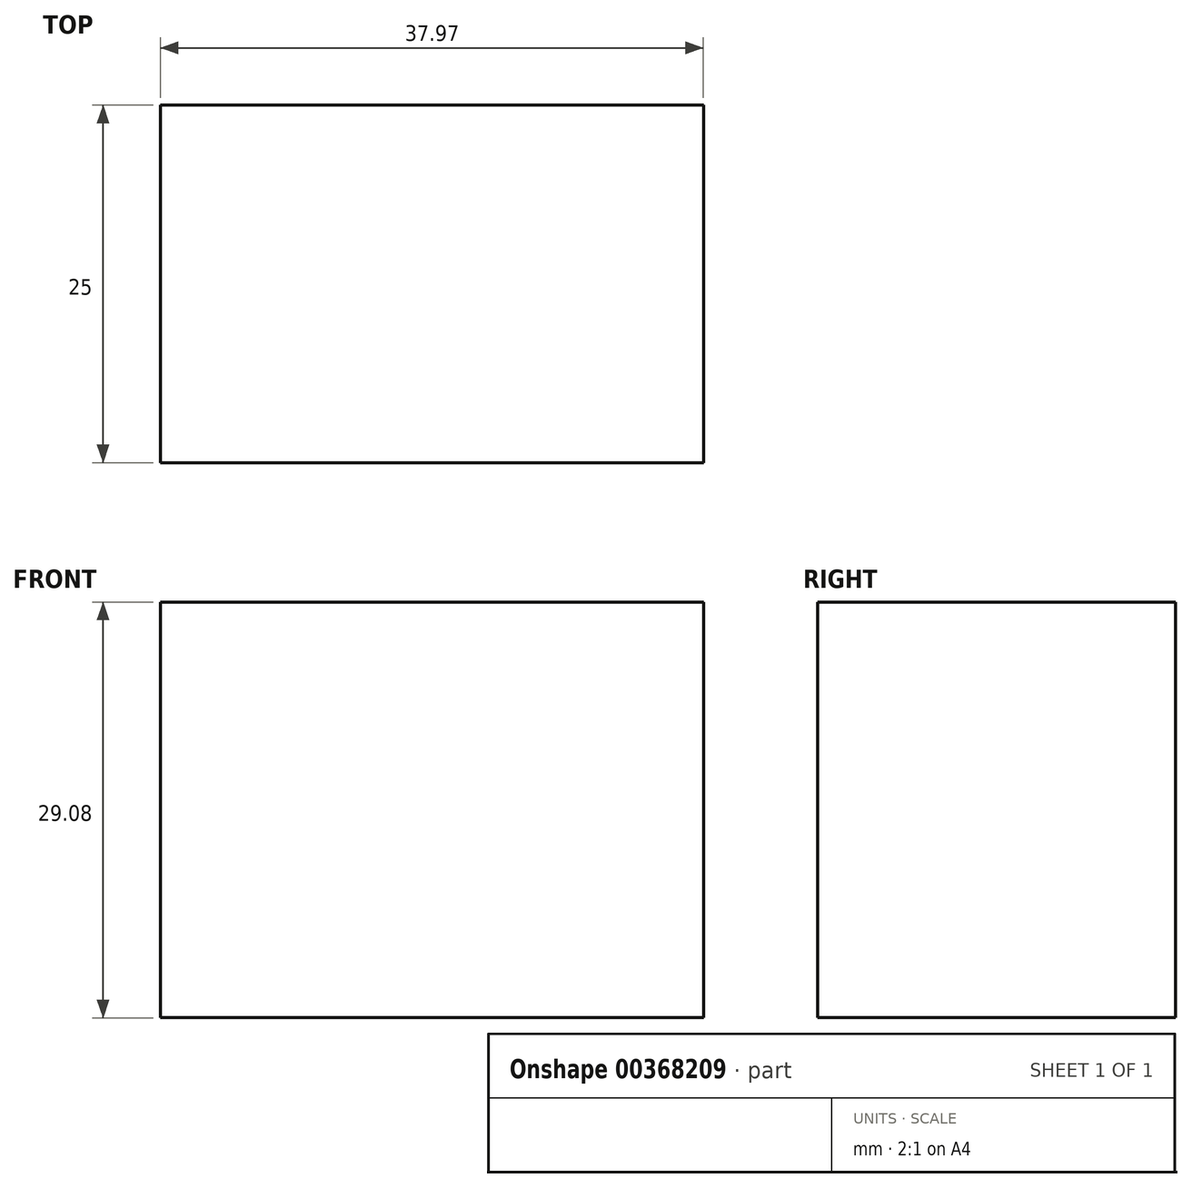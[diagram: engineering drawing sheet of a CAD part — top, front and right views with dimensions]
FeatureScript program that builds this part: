
annotation { "Feature Type Name" : "Feature", "Feature Type Description" : "" }
export const myFeature = defineFeature(function(context is Context, id is Id, definition is map)
    precondition{}
    {
        {
            var Q0;
            Q0=qCreatedBy(makeId("Front.planeOp"),FACE);
            var sketch = newSketch(context, id + "F0", { "sketchPlane" : qUnion([Q0])});
            skLineSegment(sketch, "E0.bottom", {"start": v(-30.45, 55.73) * mm, "end": v(7.52, 55.73) * mm});
            skLineSegment(sketch, "E0.top", {"start": v(-30.45, 26.65) * mm, "end": v(7.52, 26.65) * mm});
            skLineSegment(sketch, "E0.left", {"start": v(-30.45, 55.73) * mm, "end": v(-30.45, 26.65) * mm});
            skLineSegment(sketch, "E0.right", {"start": v(7.52, 55.73) * mm, "end": v(7.52, 26.65) * mm});
            skSolve(sketch);
        }
        {
            var Q0;
            Q0=makeQuery(id+"F0.imprint","IMPRINT",FACE,{"disambiguationData":[TD([[makeQuery(id+"F0.imprint","IMPRINT",EDGE,{"derivedFrom":sQuery(id+"F0.wireOp",EDGE,"E0.bottom")}),-1.0]])]});
            extrude(context, id + "F1", {"entities" : qUnion([Q0]), "depth" : 25 * mm});
        }
    });
